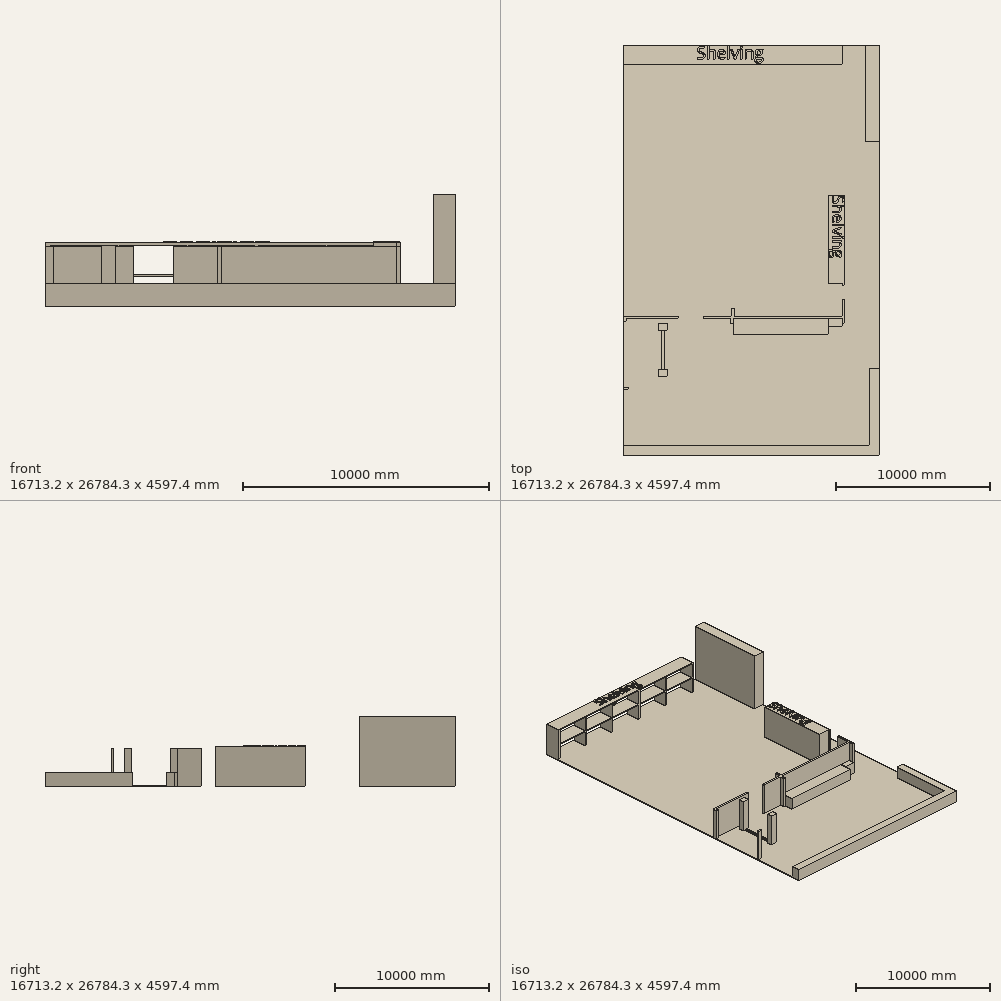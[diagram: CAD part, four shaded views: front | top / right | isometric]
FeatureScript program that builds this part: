
annotation { "Feature Type Name" : "Feature", "Feature Type Description" : "" }
export const myFeature = defineFeature(function(context is Context, id is Id, definition is map)
    precondition{}
    {
        {
            var Q0;
            Q0=qCreatedBy(makeId("Top.planeOp"),FACE);
            var sketch = newSketch(context, id + "F0", { "sketchPlane" : qUnion([Q0])});
            skLineSegment(sketch, "E0.bottom", {"start": v(8356.6, 13188.95) * mm, "end": v(-8356.6, 13188.95) * mm});
            skLineSegment(sketch, "E0.top", {"start": v(8356.6, -13188.95) * mm, "end": v(-8356.6, -13188.95) * mm});
            skLineSegment(sketch, "E0.left", {"start": v(8356.6, 13188.95) * mm, "end": v(8356.6, -13188.95) * mm});
            skLineSegment(sketch, "E0.right", {"start": v(-8356.6, 13188.95) * mm, "end": v(-8356.6, -13188.95) * mm});
            skPoint(sketch, "E0.middle", {"position": v(0, 0) * mm});
            skLineSegment(sketch, "E1.bottom", {"start": v(-8356.6, 13188.95) * mm, "end": v(8356.6, 13188.95) * mm});
            skLineSegment(sketch, "E1.top", {"start": v(-8356.6, 13595.35) * mm, "end": v(8356.6, 13595.35) * mm});
            skLineSegment(sketch, "E1.left", {"start": v(-8356.6, 13188.95) * mm, "end": v(-8356.6, 13595.35) * mm});
            skLineSegment(sketch, "E1.right", {"start": v(8356.6, 13188.95) * mm, "end": v(8356.6, 13595.35) * mm});
            skSolve(sketch);
        }
        {
            var Q0;
            Q0 = qSketchRegion(id + "F0", true);
            extrude(context, id + "F1", {"entities" : qUnion([Q0]), "depth" : 25.4 * mm});
        }
        {
            var Q0;
            Q0=makeQuery(id+"F1.opExtrude","CAP_FACE",FACE,{"disambiguationData":[OSD([sQuery(id+"F0.wireOp",EDGE,"E0.bottom"),sQuery(id+"F0.wireOp",EDGE,"E0.top"),sQuery(id+"F0.wireOp",EDGE,"E0.left"),sQuery(id+"F0.wireOp",EDGE,"E0.right")])],"isStart":false});
            var sketch = newSketch(context, id + "F2", { "sketchPlane" : qUnion([Q0])});
            skLineSegment(sketch, "E2.bottom", {"start": v(8356.6, 13595.35) * mm, "end": v(7467.6, 13595.35) * mm});
            skLineSegment(sketch, "E2.top", {"start": v(8356.6, 7321.55) * mm, "end": v(7467.6, 7321.55) * mm});
            skLineSegment(sketch, "E2.left", {"start": v(8356.6, 13595.35) * mm, "end": v(8356.6, 7321.55) * mm});
            skLineSegment(sketch, "E2.right", {"start": v(7467.6, 13595.35) * mm, "end": v(7467.6, 7321.55) * mm});
            skSolve(sketch);
        }
        {
            var Q0;
            Q0=makeQuery(id+"F2.imprint","IMPRINT",FACE,{"disambiguationData":[TD([[makeQuery(id+"F2.imprint","IMPRINT",EDGE,{"derivedFrom":sQuery(id+"F2.wireOp",EDGE,"E2.bottom")}),-1.0]])]});
            extrude(context, id + "F3", {"entities" : qUnion([Q0]), "operationType" : NewBodyOperationType.ADD, "depth" : 4572 * mm});
        }
        {
            var Q0;
            Q0=makeQuery(id+"F1.opExtrude","CAP_FACE",FACE,{"disambiguationData":[OSD([sQuery(id+"F0.wireOp",EDGE,"E0.bottom"),sQuery(id+"F0.wireOp",EDGE,"E0.top"),sQuery(id+"F0.wireOp",EDGE,"E0.left"),sQuery(id+"F0.wireOp",EDGE,"E0.right")])],"isStart":false});
            var sketch = newSketch(context, id + "F4", { "sketchPlane" : qUnion([Q0])});
            skLineSegment(sketch, "E3.top", {"start": v(-8356.6, 12350.75) * mm, "end": v(5943.6, 12350.75) * mm});
            skLineSegment(sketch, "E3.left", {"start": v(-8356.6, 13188.95) * mm, "end": v(-8356.6, 12350.75) * mm});
            skLineSegment(sketch, "E3.right", {"start": v(5943.6, 13569.95) * mm, "end": v(5943.6, 12350.75) * mm});
            skLineSegment(sketch, "E4.top", {"start": v(-8356.6, 13569.95) * mm, "end": v(5943.6, 13569.95) * mm});
            skLineSegment(sketch, "E4.left", {"start": v(-8356.6, 12350.75) * mm, "end": v(-8356.6, 13569.95) * mm});
            skLineSegment(sketch, "E4.right", {"start": v(5943.6, 12350.75) * mm, "end": v(5943.6, 13569.95) * mm});
            skSolve(sketch);
        }
        {
            var Q0;
            Q0 = qSketchRegion(id + "F4", true);
            extrude(context, id + "F5", {"entities" : qUnion([Q0]), "operationType" : NewBodyOperationType.ADD, "depth" : 2590.8 * mm});
        }
        {
            var Q0;
            Q0=makeQuery(id+"F1.opExtrude","CAP_FACE",FACE,{"disambiguationData":[OSD([sQuery(id+"F0.wireOp",EDGE,"E0.bottom"),sQuery(id+"F0.wireOp",EDGE,"E0.top"),sQuery(id+"F0.wireOp",EDGE,"E0.left"),sQuery(id+"F0.wireOp",EDGE,"E0.right")])],"isStart":false});
            var sketch = newSketch(context, id + "F6", { "sketchPlane" : qUnion([Q0])});
            skLineSegment(sketch, "E5.bottom", {"start": v(5003.8, 3816.35) * mm, "end": v(6096, 3816.35) * mm});
            skLineSegment(sketch, "E5.top", {"start": v(5943.6, -2076.45) * mm, "end": v(6096, -2076.45) * mm});
            skLineSegment(sketch, "E5.left", {"start": v(5003.8, 3816.35) * mm, "end": v(5003.8, -1974.85) * mm});
            skLineSegment(sketch, "E5.right", {"start": v(6096, 3816.35) * mm, "end": v(6096, -2076.45) * mm});
            skLineSegment(sketch, "E6.top", {"start": v(5003.8, -1974.85) * mm, "end": v(5943.6, -1974.85) * mm});
            skLineSegment(sketch, "E6.right", {"start": v(5943.6, -2076.45) * mm, "end": v(5943.6, -1974.85) * mm});
            skSolve(sketch);
        }
        {
            var Q0;
            Q0 = qSketchRegion(id + "F6", true);
            extrude(context, id + "F7", {"entities" : qUnion([Q0]), "operationType" : NewBodyOperationType.ADD, "depth" : 2590.8 * mm});
        }
        {
            var Q0;
            Q0=makeQuery(id+"F1.opExtrude","CAP_FACE",FACE,{"disambiguationData":[OSD([sQuery(id+"F0.wireOp",EDGE,"E0.bottom"),sQuery(id+"F0.wireOp",EDGE,"E0.top"),sQuery(id+"F0.wireOp",EDGE,"E0.left"),sQuery(id+"F0.wireOp",EDGE,"E0.right")])],"isStart":false});
            var sketch = newSketch(context, id + "F8", { "sketchPlane" : qUnion([Q0])});
            skLineSegment(sketch, "E7.bottom", {"start": v(6096, -2965.45) * mm, "end": v(5943.6, -2965.45) * mm});
            skLineSegment(sketch, "E7.top", {"start": v(6096, -4108.45) * mm, "end": v(5943.6, -4108.45) * mm});
            skLineSegment(sketch, "E7.left", {"start": v(6096, -2965.45) * mm, "end": v(6096, -4108.45) * mm});
            skLineSegment(sketch, "E7.right", {"start": v(5943.6, -2965.45) * mm, "end": v(5943.6, -4108.45) * mm});
            skLineSegment(sketch, "E8.bottom", {"start": v(6096, -4108.45) * mm, "end": v(-3130.55, -4108.45) * mm});
            skLineSegment(sketch, "E8.top", {"start": v(6096, -4260.85) * mm, "end": v(-3130.55, -4260.85) * mm});
            skLineSegment(sketch, "E8.left", {"start": v(6096, -4108.45) * mm, "end": v(6096, -4260.85) * mm});
            skLineSegment(sketch, "E8.right", {"start": v(-3130.55, -4108.45) * mm, "end": v(-3130.55, -4260.85) * mm});
            skLineSegment(sketch, "E9.bottom", {"start": v(6096, -4260.85) * mm, "end": v(5943.6, -4260.85) * mm});
            skLineSegment(sketch, "E9.top", {"start": v(6096, -4591.05) * mm, "end": v(5943.6, -4591.05) * mm});
            skLineSegment(sketch, "E9.left", {"start": v(6096, -4260.85) * mm, "end": v(6096, -4591.05) * mm});
            skLineSegment(sketch, "E9.right", {"start": v(5943.6, -4260.85) * mm, "end": v(5943.6, -4591.05) * mm});
            skLineSegment(sketch, "E10.bottom", {"start": v(-8356.6, -4108.45) * mm, "end": v(-4787.9, -4108.45) * mm});
            skLineSegment(sketch, "E10.top", {"start": v(-8356.6, -4260.85) * mm, "end": v(-4787.9, -4260.85) * mm});
            skLineSegment(sketch, "E10.left", {"start": v(-8356.6, -4108.45) * mm, "end": v(-8356.6, -4260.85) * mm});
            skLineSegment(sketch, "E10.right", {"start": v(-4787.9, -4108.45) * mm, "end": v(-4787.9, -4260.85) * mm});
            skLineSegment(sketch, "E11.bottom", {"start": v(-1352.55, -4260.85) * mm, "end": v(-1200.15, -4260.85) * mm});
            skLineSegment(sketch, "E11.top", {"start": v(-1352.55, -4591.05) * mm, "end": v(-1200.15, -4591.05) * mm});
            skLineSegment(sketch, "E11.left", {"start": v(-1352.55, -4260.85) * mm, "end": v(-1352.55, -4591.05) * mm});
            skLineSegment(sketch, "E11.right", {"start": v(-1200.15, -4260.85) * mm, "end": v(-1200.15, -4591.05) * mm});
            skLineSegment(sketch, "E12.bottom", {"start": v(-1276.35, -4108.45) * mm, "end": v(-1123.95, -4108.45) * mm});
            skLineSegment(sketch, "E12.top", {"start": v(-1276.35, -3587.75) * mm, "end": v(-1123.95, -3587.75) * mm});
            skLineSegment(sketch, "E12.left", {"start": v(-1276.35, -4108.45) * mm, "end": v(-1276.35, -3587.75) * mm});
            skLineSegment(sketch, "E12.right", {"start": v(-1123.95, -4108.45) * mm, "end": v(-1123.95, -3587.75) * mm});
            skLineSegment(sketch, "E13.bottom", {"start": v(-8356.6, -4260.85) * mm, "end": v(-8153.4, -4260.85) * mm});
            skLineSegment(sketch, "E13.top", {"start": v(-8356.6, -4464.05) * mm, "end": v(-8153.4, -4464.05) * mm});
            skLineSegment(sketch, "E13.left", {"start": v(-8356.6, -4260.85) * mm, "end": v(-8356.6, -4464.05) * mm});
            skLineSegment(sketch, "E13.right", {"start": v(-8153.4, -4260.85) * mm, "end": v(-8153.4, -4464.05) * mm});
            skLineSegment(sketch, "E14.bottom", {"start": v(-8356.6, -8756.65) * mm, "end": v(-8026.4, -8756.65) * mm});
            skLineSegment(sketch, "E14.top", {"start": v(-8356.6, -8909.05) * mm, "end": v(-8026.4, -8909.05) * mm});
            skLineSegment(sketch, "E14.left", {"start": v(-8356.6, -8756.65) * mm, "end": v(-8356.6, -8909.05) * mm});
            skLineSegment(sketch, "E14.right", {"start": v(-8026.4, -8756.65) * mm, "end": v(-8026.4, -8909.05) * mm});
            skSolve(sketch);
        }
        {
            var Q0;
            Q0 = qSketchRegion(id + "F8", true);
            extrude(context, id + "F9", {"entities" : qUnion([Q0]), "operationType" : NewBodyOperationType.ADD, "depth" : 2438.4 * mm});
        }
        {
            var Q0;
            Q0=makeQuery(id+"F1.opExtrude","CAP_FACE",FACE,{"disambiguationData":[OSD([sQuery(id+"F0.wireOp",EDGE,"E0.bottom"),sQuery(id+"F0.wireOp",EDGE,"E0.top"),sQuery(id+"F0.wireOp",EDGE,"E0.left"),sQuery(id+"F0.wireOp",EDGE,"E0.right")])],"isStart":false});
            var sketch = newSketch(context, id + "F10", { "sketchPlane" : qUnion([Q0])});
            skLineSegment(sketch, "E15.bottom", {"start": v(-8356.6, -13188.95) * mm, "end": v(8356.6, -13188.95) * mm});
            skLineSegment(sketch, "E15.top", {"start": v(-8356.6, -12541.25) * mm, "end": v(8356.6, -12541.25) * mm});
            skLineSegment(sketch, "E15.left", {"start": v(-8356.6, -13188.95) * mm, "end": v(-8356.6, -12541.25) * mm});
            skLineSegment(sketch, "E15.right", {"start": v(8356.6, -13188.95) * mm, "end": v(8356.6, -12541.25) * mm});
            skLineSegment(sketch, "E16.bottom", {"start": v(8356.6, -12541.25) * mm, "end": v(7708.9, -12541.25) * mm});
            skLineSegment(sketch, "E16.top", {"start": v(8356.6, -7537.45) * mm, "end": v(7708.9, -7537.45) * mm});
            skLineSegment(sketch, "E16.left", {"start": v(8356.6, -12541.25) * mm, "end": v(8356.6, -7537.45) * mm});
            skLineSegment(sketch, "E16.right", {"start": v(7708.9, -12541.25) * mm, "end": v(7708.9, -7537.45) * mm});
            skLineSegment(sketch, "E17.bottom", {"start": v(-1174.75, -4260.85) * mm, "end": v(5029.2, -4260.85) * mm});
            skLineSegment(sketch, "E17.top", {"start": v(-1174.75, -5276.85) * mm, "end": v(5029.2, -5276.85) * mm});
            skLineSegment(sketch, "E17.left", {"start": v(-1174.75, -4260.85) * mm, "end": v(-1174.75, -5276.85) * mm});
            skLineSegment(sketch, "E17.right", {"start": v(5029.2, -4260.85) * mm, "end": v(5029.2, -5276.85) * mm});
            skLineSegment(sketch, "E18.bottom", {"start": v(5054.6, -4260.85) * mm, "end": v(5918.2, -4260.85) * mm});
            skLineSegment(sketch, "E18.top", {"start": v(5054.6, -4768.85) * mm, "end": v(5918.2, -4768.85) * mm});
            skLineSegment(sketch, "E18.left", {"start": v(5054.6, -4260.85) * mm, "end": v(5054.6, -4768.85) * mm});
            skLineSegment(sketch, "E18.right", {"start": v(5918.2, -4260.85) * mm, "end": v(5918.2, -4768.85) * mm});
            skSolve(sketch);
        }
        {
            var Q0;
            Q0 = qSketchRegion(id + "F10", true);
            extrude(context, id + "F11", {"entities" : qUnion([Q0]), "operationType" : NewBodyOperationType.ADD, "depth" : 914.4 * mm});
        }
        {
            var Q0;
            Q0=makeQuery(id+"F5.opExtrude","CAP_FACE",FACE,{"disambiguationData":[OSD([sQuery(id+"F4.wireOp",EDGE,"E3.top"),sQuery(id+"F4.wireOp",EDGE,"E4.top"),sQuery(id+"F4.wireOp",EDGE,"E4.left"),sQuery(id+"F4.wireOp",EDGE,"E4.right")])],"isStart":false});
            var sketch = newSketch(context, id + "F12", { "sketchPlane" : qUnion([Q0])});
            skText(sketch, "E19", { "text": "Shelving", "fontName": "OpenSans-Regular.ttf"});
            skText(sketch, "E20", { "text": "Shelving\n", "fontName": "OpenSans-Regular.ttf"});
            const initialGuessF12  = {"E19": [-3.58263, 12.70635, 1, 0, 0.8128], "E20": [5.2832, 3.81635, 0, -1, 0.762]};
            skSetInitialGuess(sketch, initialGuessF12);
            skSolve(sketch);
        }
        {
            var Q0;
            Q0 = qSketchRegion(id + "F12", true);
            extrude(context, id + "F13", {"entities" : qUnion([Q0]), "operationType" : NewBodyOperationType.ADD, "depth" : 50.8 * mm, "hasDraft" : true, "draftAngle" : 10 * degree});
        }
        {
            var Q0;
            Q0=makeQuery(id+"F5.opExtrude","SWEPT_FACE",FACE,{"disambiguationData":[OSD([sQuery(id+"F4.wireOp",EDGE,"E3.top")])]});
            var sketch = newSketch(context, id + "F14", { "sketchPlane" : qUnion([Q0])});
            skLineSegment(sketch, "E21.bottom", {"start": v(-2546.35, 25.4) * mm, "end": v(171.45, 25.4) * mm});
            skLineSegment(sketch, "E21.top", {"start": v(-2546.35, 1244.6) * mm, "end": v(171.45, 1244.6) * mm});
            skLineSegment(sketch, "E21.left", {"start": v(-2546.35, 25.4) * mm, "end": v(-2546.35, 1244.6) * mm});
            skLineSegment(sketch, "E21.right", {"start": v(171.45, 25.4) * mm, "end": v(171.45, 1244.6) * mm});
            skLineSegment(sketch, "E22.bottom", {"start": v(171.45, 1327.15) * mm, "end": v(-2546.35, 1327.15) * mm});
            skLineSegment(sketch, "E22.top", {"start": v(171.45, 2520.95) * mm, "end": v(-2546.35, 2520.95) * mm});
            skLineSegment(sketch, "E22.left", {"start": v(171.45, 1327.15) * mm, "end": v(171.45, 2520.95) * mm});
            skLineSegment(sketch, "E22.right", {"start": v(-2546.35, 1327.15) * mm, "end": v(-2546.35, 2520.95) * mm});
            skLineSegment(sketch, "E23.1.0.0", {"start": v(-2628.9, 2520.95) * mm, "end": v(-5346.7, 2520.95) * mm});
            skLineSegment(sketch, "E23.1.0.1", {"start": v(-2628.9, 1327.15) * mm, "end": v(-5346.7, 1327.15) * mm});
            skLineSegment(sketch, "E23.1.0.2", {"start": v(-5346.7, 25.4) * mm, "end": v(-2628.9, 25.4) * mm});
            skLineSegment(sketch, "E23.1.0.3", {"start": v(-2628.9, 25.4) * mm, "end": v(-2628.9, 1244.6) * mm});
            skLineSegment(sketch, "E23.1.0.4", {"start": v(-5346.7, 25.4) * mm, "end": v(-5346.7, 1244.6) * mm});
            skLineSegment(sketch, "E23.1.0.5", {"start": v(-5346.7, 1244.6) * mm, "end": v(-2628.9, 1244.6) * mm});
            skLineSegment(sketch, "E23.1.0.6", {"start": v(-2628.9, 1327.15) * mm, "end": v(-2628.9, 2520.95) * mm});
            skLineSegment(sketch, "E23.1.0.7", {"start": v(-5346.7, 1327.15) * mm, "end": v(-5346.7, 2520.95) * mm});
            skLineSegment(sketch, "E23.2.0.0", {"start": v(-5429.25, 2520.95) * mm, "end": v(-8147.05, 2520.95) * mm});
            skLineSegment(sketch, "E23.2.0.1", {"start": v(-5429.25, 1327.15) * mm, "end": v(-8147.05, 1327.15) * mm});
            skLineSegment(sketch, "E23.2.0.2", {"start": v(-8147.05, 25.4) * mm, "end": v(-5429.25, 25.4) * mm});
            skLineSegment(sketch, "E23.2.0.3", {"start": v(-5429.25, 25.4) * mm, "end": v(-5429.25, 1244.6) * mm});
            skLineSegment(sketch, "E23.2.0.4", {"start": v(-8147.05, 25.4) * mm, "end": v(-8147.05, 1244.6) * mm});
            skLineSegment(sketch, "E23.2.0.5", {"start": v(-8147.05, 1244.6) * mm, "end": v(-5429.25, 1244.6) * mm});
            skLineSegment(sketch, "E23.2.0.6", {"start": v(-5429.25, 1327.15) * mm, "end": v(-5429.25, 2520.95) * mm});
            skLineSegment(sketch, "E23.2.0.7", {"start": v(-8147.05, 1327.15) * mm, "end": v(-8147.05, 2520.95) * mm});
            skLineSegment(sketch, "E23.direction1", {"start": v(-2546.35, 25.4) * mm, "end": v(-5346.7, 25.4) * mm, "construction": true});
            skLineSegment(sketch, "E24.1.0.0", {"start": v(3060.7, 2520.95) * mm, "end": v(342.9, 2520.95) * mm});
            skLineSegment(sketch, "E24.1.0.1", {"start": v(3060.7, 1327.15) * mm, "end": v(3060.7, 2520.95) * mm});
            skLineSegment(sketch, "E24.1.0.2", {"start": v(3060.7, 25.4) * mm, "end": v(3060.7, 1244.6) * mm});
            skLineSegment(sketch, "E24.1.0.3", {"start": v(3060.7, 1327.15) * mm, "end": v(342.9, 1327.15) * mm});
            skLineSegment(sketch, "E24.1.0.4", {"start": v(342.9, 1244.6) * mm, "end": v(3060.7, 1244.6) * mm});
            skLineSegment(sketch, "E24.1.0.5", {"start": v(342.9, 1327.15) * mm, "end": v(342.9, 2520.95) * mm});
            skLineSegment(sketch, "E24.1.0.6", {"start": v(342.9, 25.4) * mm, "end": v(342.9, 1244.6) * mm});
            skLineSegment(sketch, "E24.1.0.7", {"start": v(342.9, 25.4) * mm, "end": v(3060.7, 25.4) * mm});
            skLineSegment(sketch, "E25.1.0.0", {"start": v(3143.25, 1327.15) * mm, "end": v(3143.25, 2520.95) * mm});
            skLineSegment(sketch, "E25.1.0.1", {"start": v(5861.05, 2520.95) * mm, "end": v(3143.25, 2520.95) * mm});
            skLineSegment(sketch, "E25.1.0.2", {"start": v(5861.05, 1327.15) * mm, "end": v(3143.25, 1327.15) * mm});
            skLineSegment(sketch, "E25.1.0.3", {"start": v(5861.05, 1327.15) * mm, "end": v(5861.05, 2520.95) * mm});
            skLineSegment(sketch, "E25.1.0.4", {"start": v(5861.05, 25.4) * mm, "end": v(5861.05, 1244.6) * mm});
            skLineSegment(sketch, "E25.1.0.5", {"start": v(3143.25, 1244.6) * mm, "end": v(5861.05, 1244.6) * mm});
            skLineSegment(sketch, "E25.1.0.6", {"start": v(3143.25, 25.4) * mm, "end": v(5861.05, 25.4) * mm});
            skLineSegment(sketch, "E25.1.0.7", {"start": v(3143.25, 25.4) * mm, "end": v(3143.25, 1244.6) * mm});
            skLineSegment(sketch, "E25.direction1", {"start": v(342.9, 1327.15) * mm, "end": v(3143.25, 1327.15) * mm, "construction": true});
            skSolve(sketch);
        }
        {
            var Q0;
            Q0 = qSketchRegion(id + "F14", true);
            extrude(context, id + "F15", {"entities" : qUnion([Q0]), "operationType" : NewBodyOperationType.REMOVE, "oppositeDirection" : true, "depth" : 1219.2 * mm});
        }
        {
            var Q0;
            Q0=makeQuery(id+"F15.boolean.opBoolean","COPY",FACE,{"derivedFrom":makeQuery(id+"F15.opExtrude","SWEPT_FACE",FACE,{"disambiguationData":[OSD([sQuery(id+"F14.wireOp",EDGE,"E22.bottom")])]})});
            var sketch = newSketch(context, id + "F16", { "sketchPlane" : qUnion([Q0])});
            skLineSegment(sketch, "E26", {"start": v(-2546.35, 13569.95) * mm, "end": v(-1187.45, 13569.95) * mm, "construction": true});
            skSolve(sketch);
        }
        {
            var Q0;
            Q0=sQuery(id+"F16.wireOp",VERTEX,"E26.end");
            var Q1;
            Q1=sQuery(id+"F16.wireOp",EDGE,"E26");
            cPlane(context, id + "F17", {"entities" : qUnion([Q0, Q1]), "cplaneType" : CPlaneType.LINE_POINT, "offset" : 25.4 * mm, "width" : 152.4 * mm, "height" : 152.4 * mm});
        }
        {
            var Q0;
            Q0=qCreatedBy(id+"F17.planeOp",FACE);
            var sketch = newSketch(context, id + "F18", { "sketchPlane" : qUnion([Q0])});
            skLineSegment(sketch, "E27", {"start": v(13569.95, 1327.15) * mm, "end": v(12350.75, 1327.15) * mm});
            skLineSegment(sketch, "E28", {"start": v(13493.75, 1327.15) * mm, "end": v(13315.95, 2520.95) * mm});
            skLineSegment(sketch, "E29.0", {"start": v(13569.95, 2520.95) * mm, "end": v(12350.75, 2520.95) * mm});
            skLineSegment(sketch, "E30", {"start": v(13569.95, 1327.15) * mm, "end": v(13569.95, 2520.95) * mm});
            skSolve(sketch);
        }
        {
            var Q0;
            Q0 = qSketchRegion(id + "F4", true);
            extrude(context, id + "F19", {"entities" : qUnion([Q0]), "operationType" : NewBodyOperationType.ADD, "oppositeDirection" : true, "depth" : 25.4 * mm});
        }
        {
            var Q0;
            Q0 = qSketchRegion(id + "F18", true);
            extrude(context, id + "F20", {"entities" : qUnion([Q0]), "operationType" : NewBodyOperationType.ADD, "endBound" : BoundingType.SYMMETRIC, "depth" : 152.4 * mm});
        }
        {
            var Q0;
            {var subQ2=sQuery(id+"F2.wireOp",EDGE,"E2.top");Q0=makeQuery(id+"F2.imprint","IMPRINT",FACE,{"disambiguationData":[TD([[makeQuery(id+"F2.imprint","IMPRINT",EDGE,{"derivedFrom":subQ2}),1.0]])]});}
            var sketch = newSketch(context, id + "F21", { "sketchPlane" : qUnion([Q0])});
            skLineSegment(sketch, "E31.bottom", {"start": v(-6070.6, -4578.35) * mm, "end": v(-5511.8, -4578.35) * mm});
            skLineSegment(sketch, "E31.top", {"start": v(-6070.6, -5010.15) * mm, "end": v(-5511.8, -5010.15) * mm});
            skLineSegment(sketch, "E31.left", {"start": v(-6070.6, -4578.35) * mm, "end": v(-6070.6, -5010.15) * mm});
            skLineSegment(sketch, "E31.right", {"start": v(-5511.8, -4578.35) * mm, "end": v(-5511.8, -5010.15) * mm});
            skLineSegment(sketch, "E32.bottom", {"start": v(-5892.8, -5010.15) * mm, "end": v(-5689.6, -5010.15) * mm});
            skLineSegment(sketch, "E32.top", {"start": v(-5892.8, -7575.55) * mm, "end": v(-5689.6, -7575.55) * mm});
            skLineSegment(sketch, "E32.left", {"start": v(-5892.8, -5010.15) * mm, "end": v(-5892.8, -7575.55) * mm});
            skLineSegment(sketch, "E32.right", {"start": v(-5689.6, -5010.15) * mm, "end": v(-5689.6, -7575.55) * mm});
            skLineSegment(sketch, "E33.bottom", {"start": v(-6070.6, -7575.55) * mm, "end": v(-5511.8, -7575.55) * mm});
            skLineSegment(sketch, "E33.top", {"start": v(-6070.6, -8007.35) * mm, "end": v(-5511.8, -8007.35) * mm});
            skLineSegment(sketch, "E33.left", {"start": v(-6070.6, -7575.55) * mm, "end": v(-6070.6, -8007.35) * mm});
            skLineSegment(sketch, "E33.right", {"start": v(-5511.8, -7575.55) * mm, "end": v(-5511.8, -8007.35) * mm});
            skPoint(sketch, "E34", {"position": v(-5791.2, -5010.15) * mm});
            skLineSegment(sketch, "E35", {"start": v(-5791.2, -5010.15) * mm, "end": v(-5791.2, -5568.23) * mm, "construction": true});
            skSolve(sketch);
        }
        {
            var Q0;
            Q0 = qSketchRegion(id + "F21", true);
            extrude(context, id + "F22", {"entities" : qUnion([Q0]), "operationType" : NewBodyOperationType.ADD, "depth" : 50.8 * mm});
        }
        {
            var Q0;
            Q0=makeQuery(id+"F22.opExtrude","CAP_FACE",FACE,{"disambiguationData":[OSD([sQuery(id+"F21.wireOp",EDGE,"E31.bottom"),sQuery(id+"F21.wireOp",EDGE,"E31.top"),sQuery(id+"F21.wireOp",EDGE,"E31.left"),sQuery(id+"F21.wireOp",EDGE,"E31.right"),sQuery(id+"F21.wireOp",EDGE,"E32.left"),sQuery(id+"F21.wireOp",EDGE,"E32.right"),sQuery(id+"F21.wireOp",EDGE,"E33.bottom"),sQuery(id+"F21.wireOp",EDGE,"E33.top"),sQuery(id+"F21.wireOp",EDGE,"E33.left"),sQuery(id+"F21.wireOp",EDGE,"E33.right")])],"isStart":false});
            var sketch = newSketch(context, id + "F23", { "sketchPlane" : qUnion([Q0])});
            skLineSegment(sketch, "E36.bottom", {"start": v(-6070.6, -4578.35) * mm, "end": v(-5511.8, -4578.35) * mm});
            skLineSegment(sketch, "E36.top", {"start": v(-6070.6, -5010.15) * mm, "end": v(-5511.8, -5010.15) * mm});
            skLineSegment(sketch, "E36.left", {"start": v(-6070.6, -4578.35) * mm, "end": v(-6070.6, -5010.15) * mm});
            skLineSegment(sketch, "E36.right", {"start": v(-5511.8, -4578.35) * mm, "end": v(-5511.8, -5010.15) * mm});
            skLineSegment(sketch, "E37.bottom", {"start": v(-6070.6, -8007.35) * mm, "end": v(-5511.8, -8007.35) * mm});
            skLineSegment(sketch, "E37.top", {"start": v(-6070.6, -7575.55) * mm, "end": v(-5511.8, -7575.55) * mm});
            skLineSegment(sketch, "E37.left", {"start": v(-6070.6, -8007.35) * mm, "end": v(-6070.6, -7575.55) * mm});
            skLineSegment(sketch, "E37.right", {"start": v(-5511.8, -8007.35) * mm, "end": v(-5511.8, -7575.55) * mm});
            skSolve(sketch);
        }
        {
            var Q0;
            Q0 = qSketchRegion(id + "F23", true);
            extrude(context, id + "F24", {"entities" : qUnion([Q0]), "operationType" : NewBodyOperationType.ADD, "depth" : 2438.4 * mm});
        }
    });
